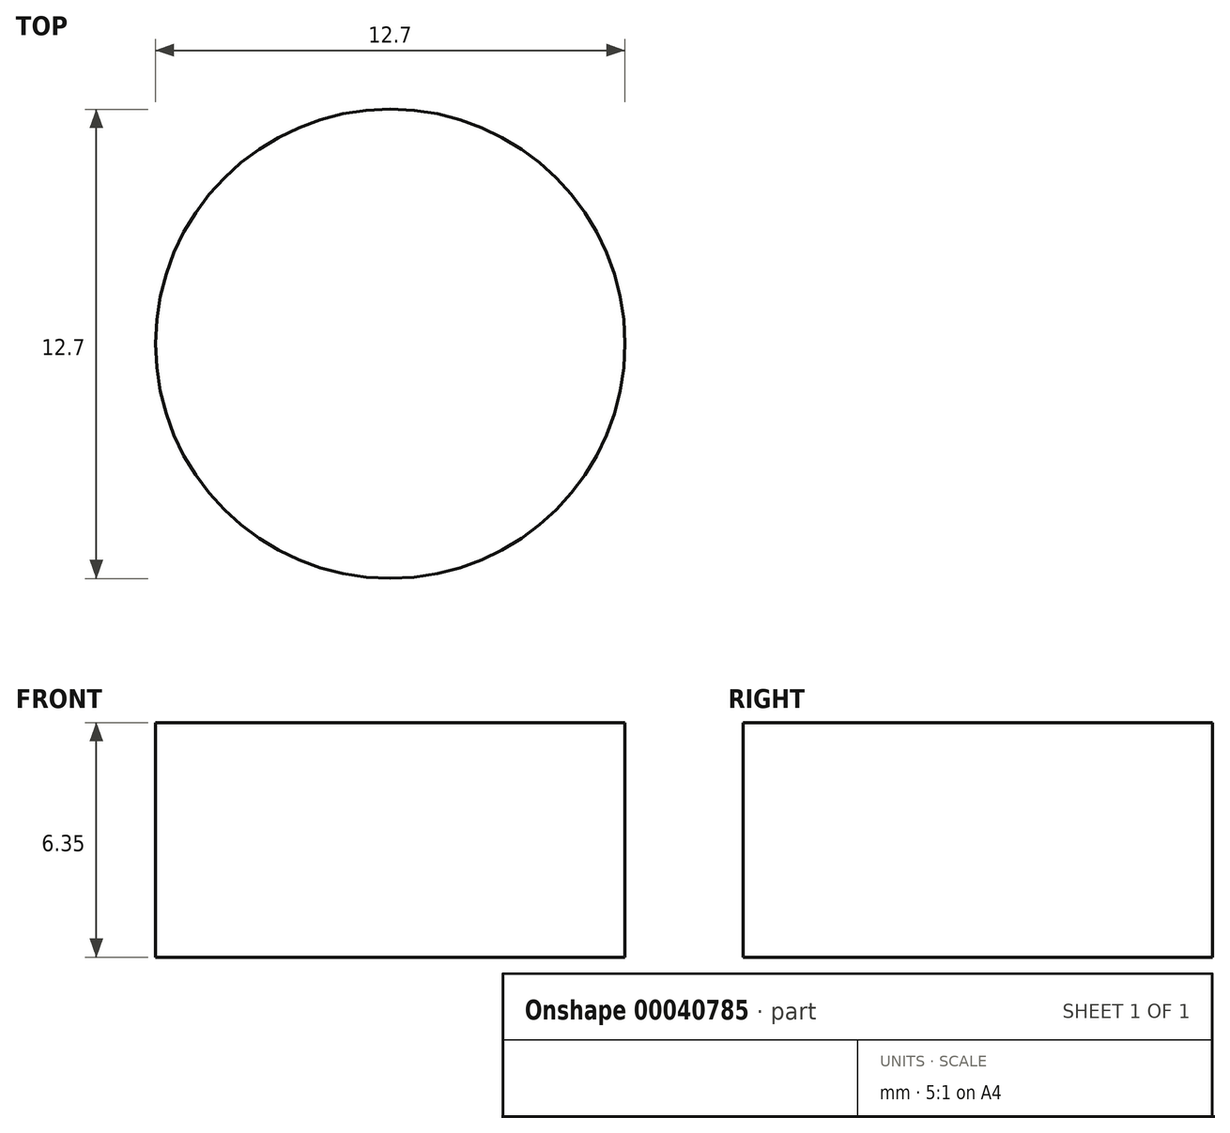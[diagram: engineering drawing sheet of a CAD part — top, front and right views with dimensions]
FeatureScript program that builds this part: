
annotation { "Feature Type Name" : "Feature", "Feature Type Description" : "" }
export const myFeature = defineFeature(function(context is Context, id is Id, definition is map)
    precondition{}
    {
        {
            var Q0;
            Q0=qCreatedBy(makeId("Top.planeOp"),FACE);
            var sketch = newSketch(context, id + "F0", { "sketchPlane" : qUnion([Q0])});
            skCircle(sketch, "E0", {"center": v(-53.16, 48.75) * mm, "radius": 6.35 * mm});
            skSolve(sketch);
        }
        {
            var Q0;
            Q0 = qSketchRegion(id + "F0", true);
            extrude(context, id + "F1", {"entities" : qUnion([Q0]), "depth" : 6.35 * mm});
        }
    });
